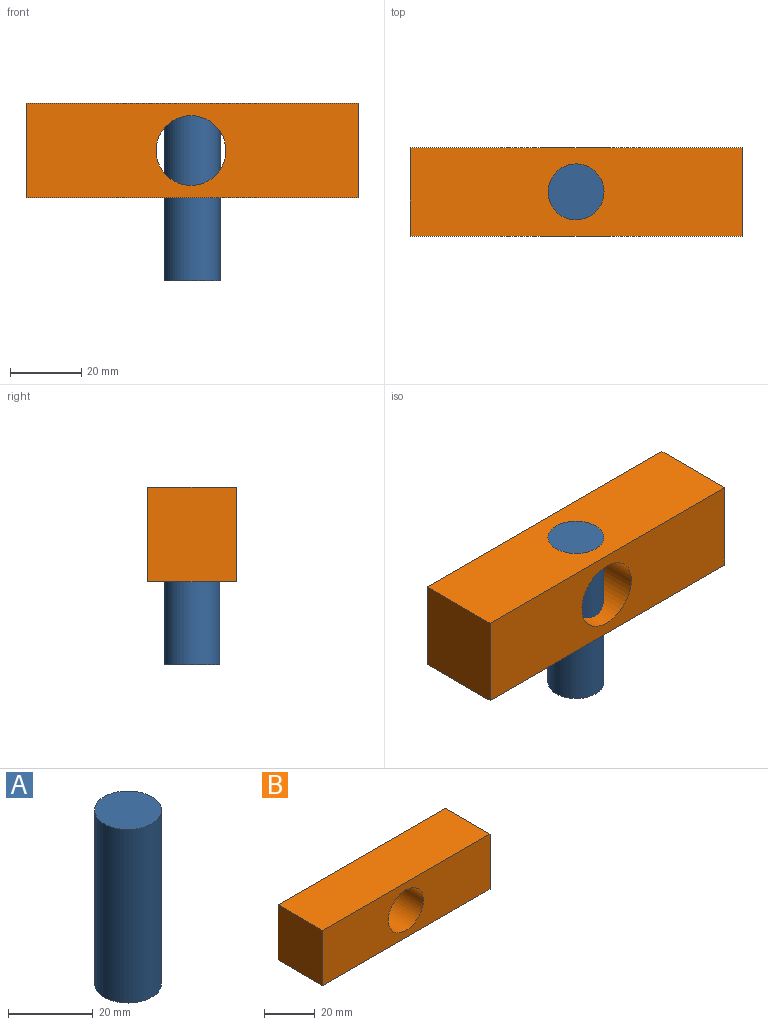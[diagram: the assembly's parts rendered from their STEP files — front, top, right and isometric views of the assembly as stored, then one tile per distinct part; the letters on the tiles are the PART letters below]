
ASSEMBLY  parts=2 mates=1
PART A: 3 faces, bbox 15.8x15.8x50 mm
  f0: cylinder r=7.88mm len=50mm, axis (0,0,-1), area 2476.6mm2, adj f1,f2
  f1: plane 15.77x15.77mm, normal (0,0,1), area 195.2mm2, adj f0
  f2: plane 15.77x15.77mm, normal (0,0,-1), area 195.2mm2, adj f0
PART B: 7 faces, bbox 93.4x25x26.7 mm
  f0: plane 93.45x25mm, normal (0,0,-1), area 2336.2mm2, adj f1,f4,f5,f6
  f1: plane 26.65x25mm, normal (1,0,0), area 666.4mm2, adj f0,f2,f5,f6
  f2: plane 93.45x25mm, normal (0,0,1), area 2336.2mm2, adj f1,f4,f5,f6
  f3: cylinder r=9.82mm len=25mm, axis (0,1,0), area 1542.3mm2, adj f5,f6
  f4: plane 26.65x25mm, normal (-1,0,0), area 666.4mm2, adj f0,f2,f5,f6
  f5: plane 93.45x26.65mm, normal (0,-1,0), area 2187.9mm2, adj f0,f1,f2,f3,f4
  f6: plane 93.45x26.65mm, normal (0,1,0), area 2187.9mm2, adj f0,f1,f2,f3,f4
PLACE A t=(-25.29,-41.95,-26.15)mm
PLACE B t=(-25.58,-21.57,-2.8)mm
MATE fastened A.f0 <-> B.f2  axis (0,0,1) through (-25.29,-34.07,23.85)mm
